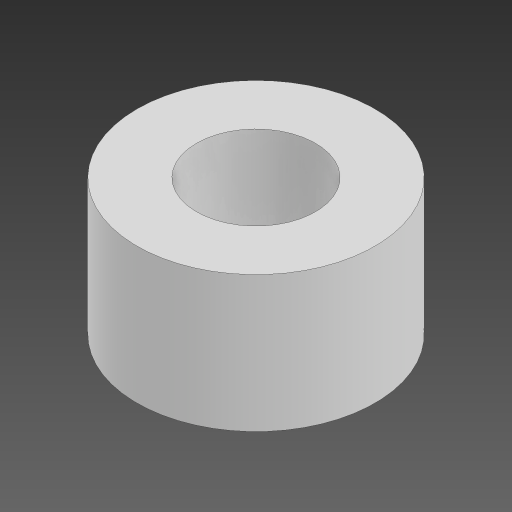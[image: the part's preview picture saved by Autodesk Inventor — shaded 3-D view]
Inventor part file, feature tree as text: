
AUTODESK INVENTOR PART (.ipt)
format: ipt  version: 2024 (Build 280153000, 153)  size: 95,232 bytes
history: native  units: mm
features: extrude x1, sketch x1
ambient origin geometry x8: Origin, YZ Plane, XZ Plane, XY Plane, X Axis, Y Axis, Z Axis, Center Point
bodies: Solid1 (feature_tree)
feature tree (2):
  extrude  "Extrusion1"  Depth=3.5mm
  sketch  "Sketch1"  dims[d0=7.0mm d1=3.5mm d2=4.0mm d3=0.0mm]
